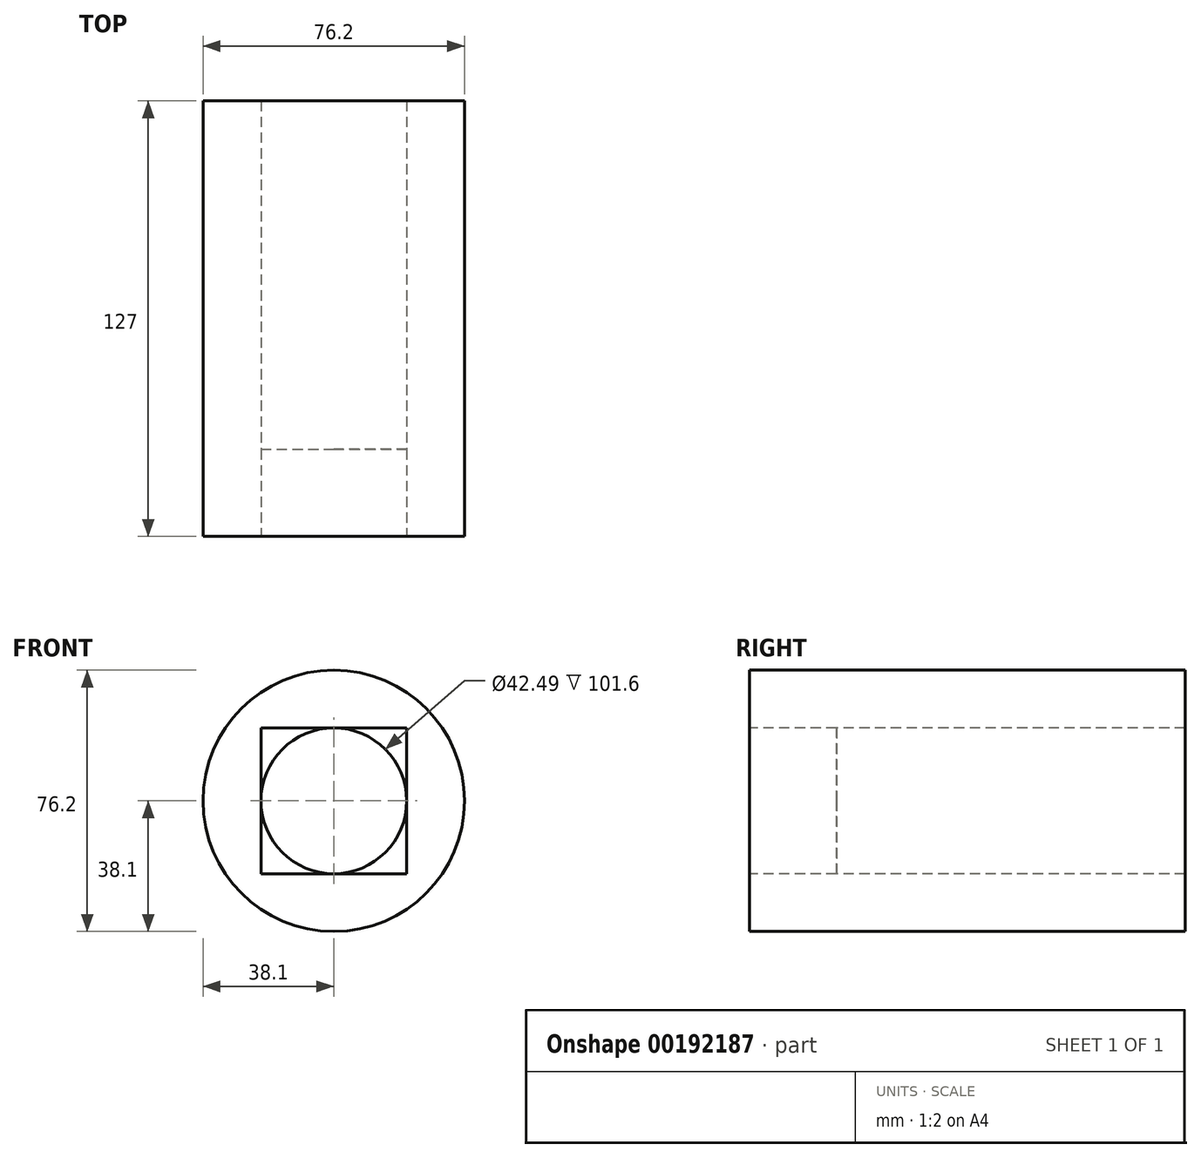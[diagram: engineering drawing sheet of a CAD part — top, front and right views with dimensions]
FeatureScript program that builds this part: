
annotation { "Feature Type Name" : "Feature", "Feature Type Description" : "" }
export const myFeature = defineFeature(function(context is Context, id is Id, definition is map)
    precondition{}
    {
        {
            var Q0;
            Q0=qCreatedBy(makeId("Front.planeOp"),FACE);
            var sketch = newSketch(context, id + "F0", { "sketchPlane" : qUnion([Q0])});
            skCircle(sketch, "E0", {"center": v(0, 0) * mm, "radius": 38.1 * mm});
            skSolve(sketch);
        }
        {
            var Q0;
            Q0=qCreatedBy(makeId("Front.planeOp"),FACE);
            var sketch = newSketch(context, id + "F1", { "sketchPlane" : qUnion([Q0])});
            skLineSegment(sketch, "E1.bottom", {"start": v(-21.25, -21.25) * mm, "end": v(21.25, -21.25) * mm});
            skLineSegment(sketch, "E1.top", {"start": v(-21.25, 21.25) * mm, "end": v(21.25, 21.25) * mm});
            skLineSegment(sketch, "E1.left", {"start": v(-21.25, -21.25) * mm, "end": v(-21.25, 21.25) * mm});
            skLineSegment(sketch, "E1.right", {"start": v(21.25, -21.25) * mm, "end": v(21.25, 21.25) * mm});
            skPoint(sketch, "E1.middle", {"position": v(0, 0) * mm});
            skSolve(sketch);
        }
        {
            var Q0;
            Q0=qCreatedBy(makeId("Front.planeOp"),FACE);
            var sketch = newSketch(context, id + "F2", { "sketchPlane" : qUnion([Q0])});
            skCircle(sketch, "E2", {"center": v(0, 0) * mm, "radius": 21.25 * mm});
            skSolve(sketch);
        }
        {
            var Q0;
            Q0 = qSketchRegion(id + "F0", true);
            extrude(context, id + "F3", {"entities" : qUnion([Q0]), "oppositeDirection" : true, "depth" : 127 * mm});
        }
        {
            var Q0;
            Q0=makeQuery(id+"F2.imprint","IMPRINT",FACE,{"disambiguationData":[TD([[makeQuery(id+"F2.imprint","IMPRINT",EDGE,{"derivedFrom":sQuery(id+"F2.wireOp",EDGE,"E2")}),1.0]])]});
            var Q1;
            Q1=sQuery(id+"F2.wireOp",EDGE,"E2");
            extrude(context, id + "F4", {"entities" : qUnion([Q0]), "operationType" : NewBodyOperationType.REMOVE, "surfaceEntities" : qUnion([Q1]), "endBound" : BoundingType.THROUGH_ALL, "oppositeDirection" : true, "depth" : 25.4 * mm});
        }
        {
            var Q0;
            Q0 = qSketchRegion(id + "F1", true);
            extrude(context, id + "F5", {"entities" : qUnion([Q0]), "operationType" : NewBodyOperationType.REMOVE, "oppositeDirection" : true, "depth" : 25.4 * mm});
        }
    });
